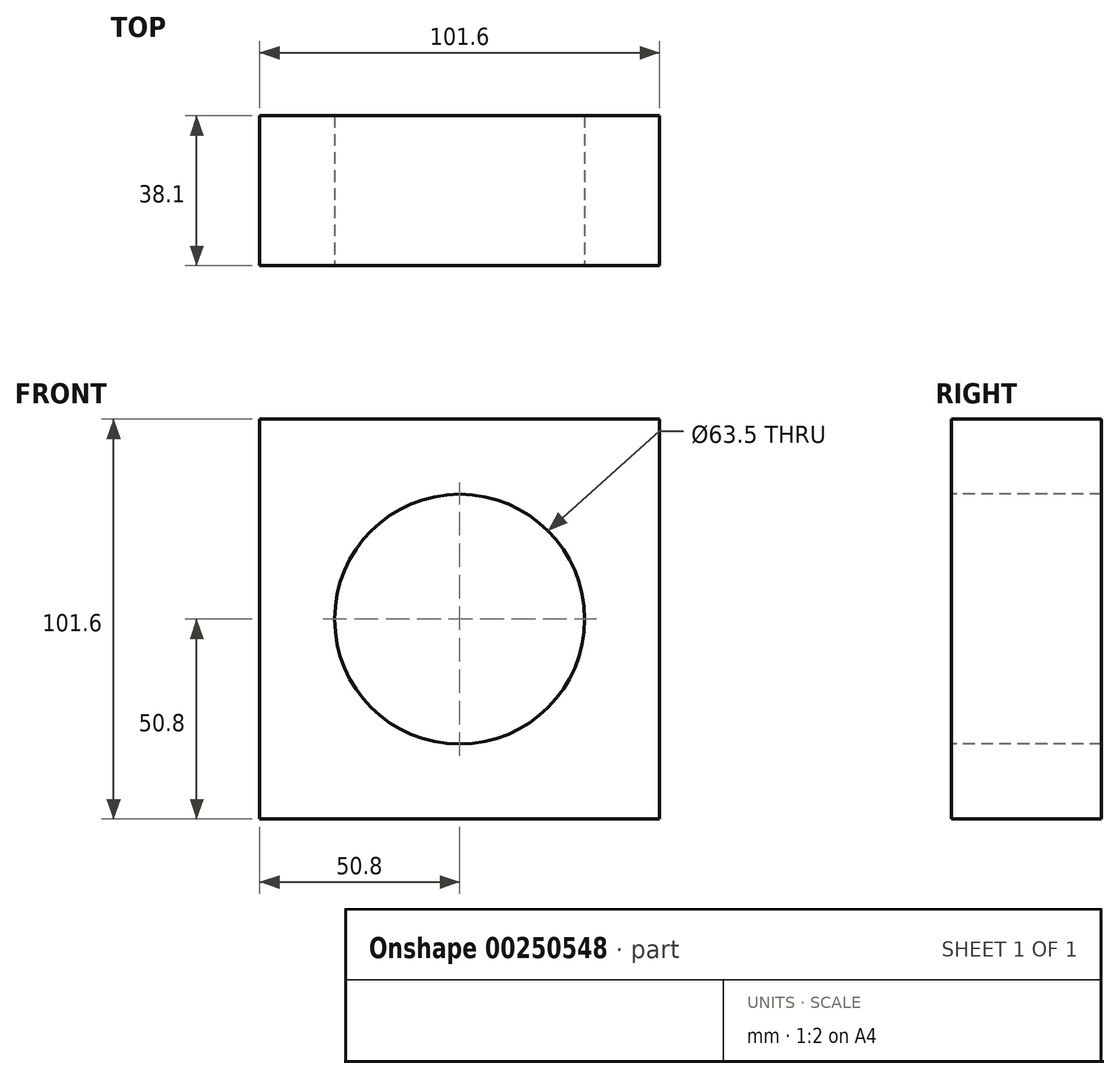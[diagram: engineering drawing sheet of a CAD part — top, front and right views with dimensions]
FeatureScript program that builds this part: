
annotation { "Feature Type Name" : "Feature", "Feature Type Description" : "" }
export const myFeature = defineFeature(function(context is Context, id is Id, definition is map)
    precondition{}
    {
        {
            var Q0;
            Q0=qCreatedBy(makeId("Front.planeOp"),FACE);
            var sketch = newSketch(context, id + "F0", { "sketchPlane" : qUnion([Q0])});
            skCircle(sketch, "E0", {"center": v(0, 0) * mm, "radius": 31.75 * mm});
            skLineSegment(sketch, "E1.bottom", {"start": v(50.8, -50.8) * mm, "end": v(-50.8, -50.8) * mm});
            skLineSegment(sketch, "E1.top", {"start": v(50.8, 50.8) * mm, "end": v(-50.8, 50.8) * mm});
            skLineSegment(sketch, "E1.left", {"start": v(50.8, -50.8) * mm, "end": v(50.8, 50.8) * mm});
            skLineSegment(sketch, "E1.right", {"start": v(-50.8, -50.8) * mm, "end": v(-50.8, 50.8) * mm});
            skLineSegment(sketch, "E2.bottom", {"start": v(76.2, -76.2) * mm, "end": v(-76.2, -76.2) * mm});
            skLineSegment(sketch, "E2.top", {"start": v(76.2, 76.2) * mm, "end": v(-76.2, 76.2) * mm});
            skLineSegment(sketch, "E2.left", {"start": v(76.2, -76.2) * mm, "end": v(76.2, 76.2) * mm});
            skLineSegment(sketch, "E2.right", {"start": v(-76.2, -76.2) * mm, "end": v(-76.2, 76.2) * mm});
            skSolve(sketch);
        }
        {
            var Q0;
            Q0=makeQuery(id+"F0.imprint","IMPRINT",FACE,{"disambiguationData":[TD([[makeQuery(id+"F0.imprint","IMPRINT",EDGE,{"derivedFrom":sQuery(id+"F0.wireOp",EDGE,"E0")}),-1.0]])]});
            extrude(context, id + "F1", {"entities" : qUnion([Q0]), "oppositeDirection" : true, "depth" : 38.1 * mm});
        }
    });
